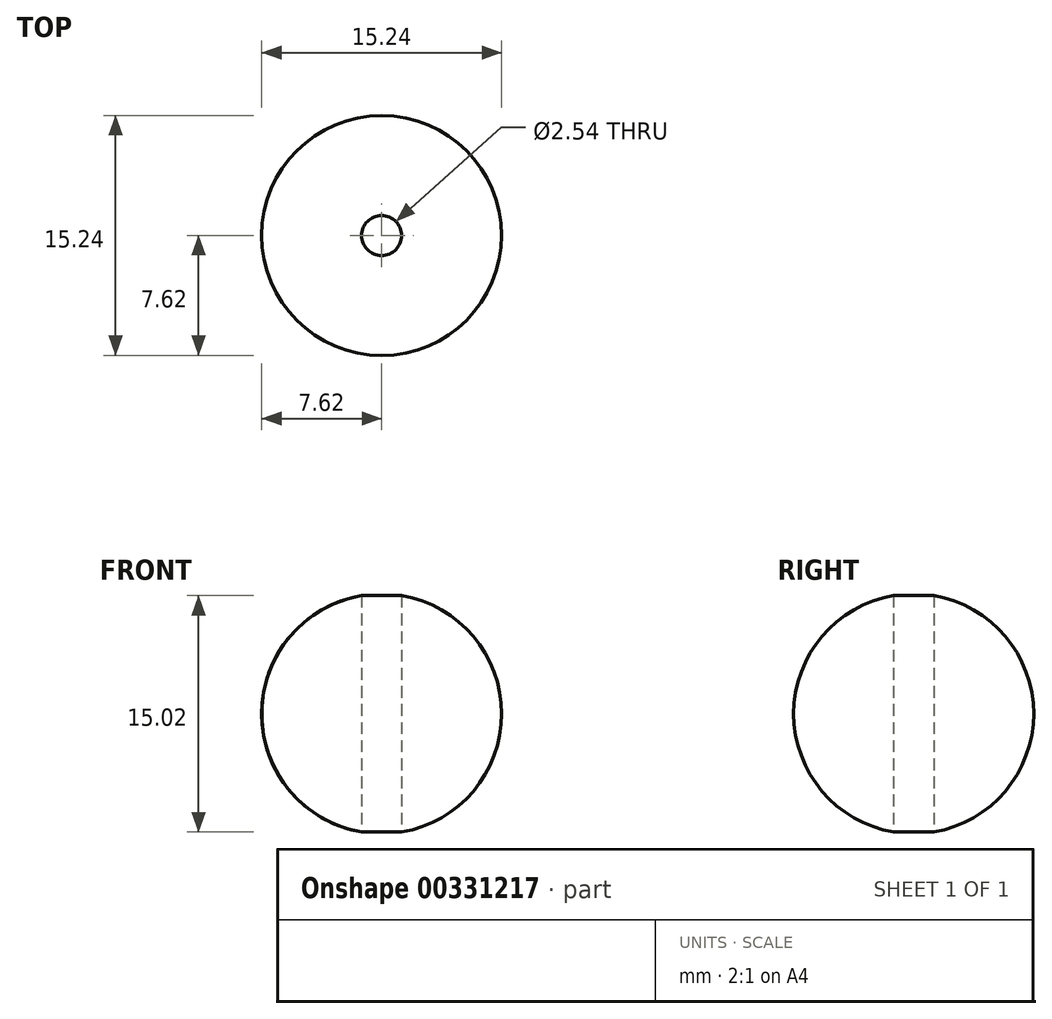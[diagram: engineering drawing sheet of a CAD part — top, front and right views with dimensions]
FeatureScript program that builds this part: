
annotation { "Feature Type Name" : "Feature", "Feature Type Description" : "" }
export const myFeature = defineFeature(function(context is Context, id is Id, definition is map)
    precondition{}
    {
        {
            var Q0;
            Q0=qCreatedBy(makeId("Front.planeOp"),FACE);
            var sketch = newSketch(context, id + "F0", { "sketchPlane" : qUnion([Q0])});
            skLineSegment(sketch, "E0", {"start": v(0, 0) * mm, "end": v(0, 48.07) * mm, "construction": true});
            skArc(sketch, "E1", {"start": v(1.27, 7.51) * mm, "mid": v(7.62, 0) * mm, "end": v(1.27, -7.51) * mm});
            skLineSegment(sketch, "E2", {"start": v(1.27, 7.51) * mm, "end": v(1.27, -7.51) * mm});
            skSolve(sketch);
        }
        {
            var Q0;
            Q0 = qSketchRegion(id + "F0", true);
            var Q1;
            Q1=sQuery(id+"F0.wireOp",EDGE,"E0");
            revolve(context, id + "F1", {"entities" : qUnion([Q0]), "axis" : qUnion([Q1]), "revolveType" : RevolveType.FULL});
        }
    });
